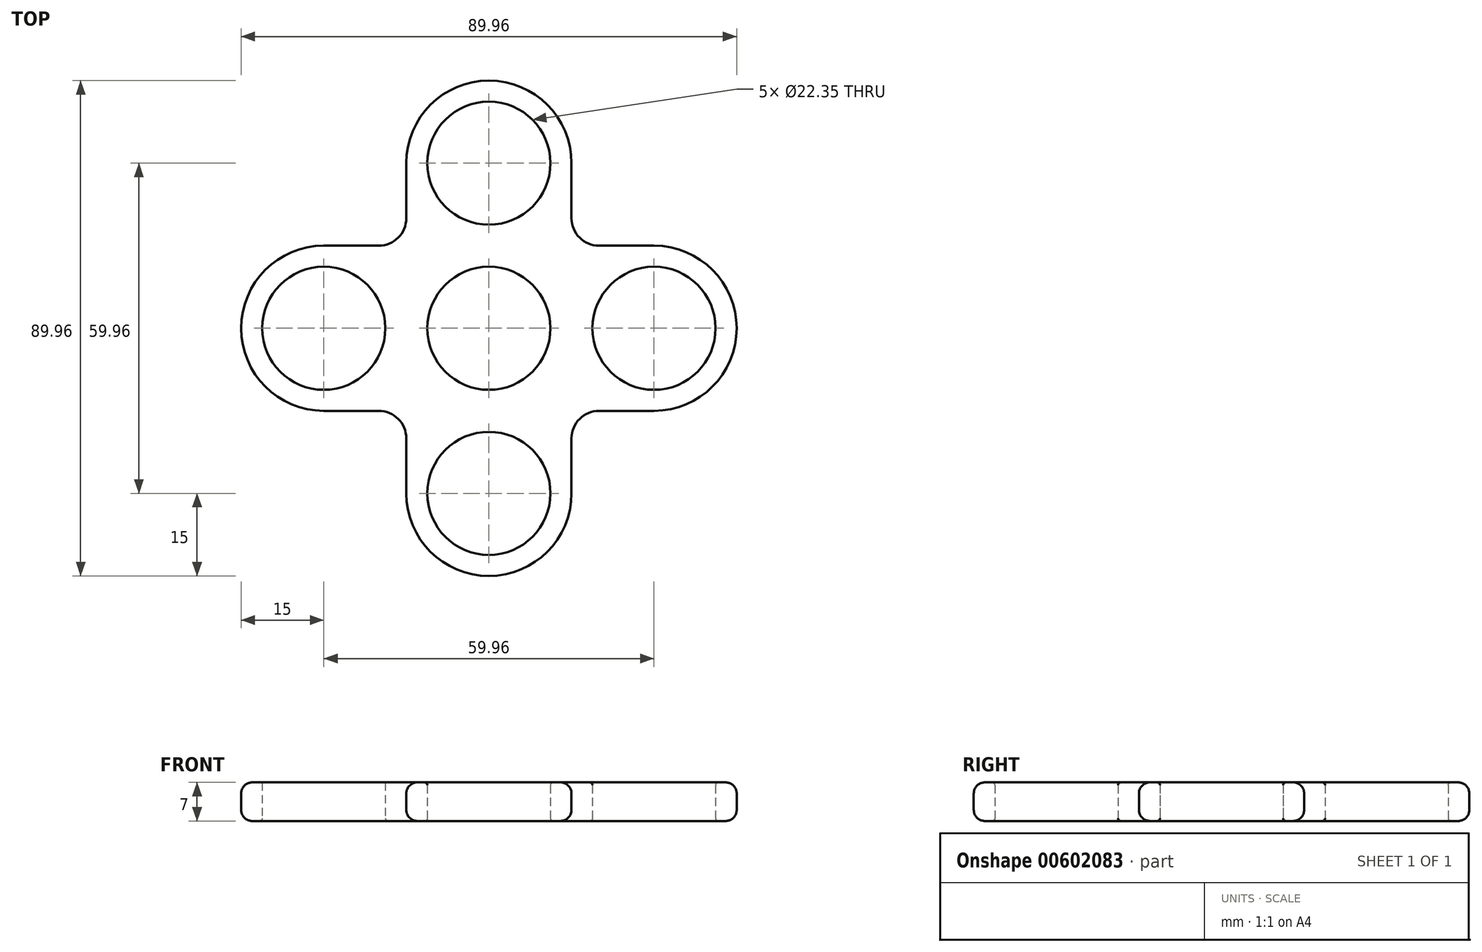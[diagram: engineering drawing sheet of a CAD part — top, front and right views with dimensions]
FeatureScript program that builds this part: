
annotation { "Feature Type Name" : "Feature", "Feature Type Description" : "" }
export const myFeature = defineFeature(function(context is Context, id is Id, definition is map)
    precondition{}
    {
        {
            var Q0;
            Q0=qCreatedBy(makeId("Top.planeOp"),FACE);
            var sketch = newSketch(context, id + "F0", { "sketchPlane" : qUnion([Q0])});
            skCircle(sketch, "E0", {"center": v(0, 29.98) * mm, "radius": 11.18 * mm});
            skLineSegment(sketch, "E1", {"start": v(0, 0) * mm, "end": v(0, 29.98) * mm, "construction": true});
            skCircle(sketch, "E2", {"center": v(0, 29.98) * mm, "radius": 15 * mm});
            skCircle(sketch, "E3", {"center": v(0, 0) * mm, "radius": 11.18 * mm});
            skLineSegment(sketch, "E4", {"start": v(-15, 29.98) * mm, "end": v(-15, 0) * mm});
            skLineSegment(sketch, "E5", {"start": v(15, 29.98) * mm, "end": v(15, 0) * mm});
            skLineSegment(sketch, "E6", {"start": v(-15, 0) * mm, "end": v(15, 0) * mm});
            skLineSegment(sketch, "E7.1.0", {"start": v(-29.98, -15) * mm, "end": v(0, -15) * mm});
            skCircle(sketch, "E7.1.1", {"center": v(-29.98, 0) * mm, "radius": 15 * mm});
            skCircle(sketch, "E7.1.2", {"center": v(-29.98, 0) * mm, "radius": 11.18 * mm});
            skLineSegment(sketch, "E7.1.3", {"start": v(-29.98, 15) * mm, "end": v(0, 15) * mm});
            skLineSegment(sketch, "E7.2.0", {"start": v(15, -29.98) * mm, "end": v(15, 0) * mm});
            skCircle(sketch, "E7.2.1", {"center": v(0, -29.98) * mm, "radius": 15 * mm});
            skCircle(sketch, "E7.2.2", {"center": v(0, -29.98) * mm, "radius": 11.18 * mm});
            skLineSegment(sketch, "E7.2.3", {"start": v(-15, -29.98) * mm, "end": v(-15, 0) * mm});
            skLineSegment(sketch, "E7.3.0", {"start": v(29.98, 15) * mm, "end": v(0, 15) * mm});
            skCircle(sketch, "E7.3.1", {"center": v(29.98, 0) * mm, "radius": 15 * mm});
            skCircle(sketch, "E7.3.2", {"center": v(29.98, 0) * mm, "radius": 11.18 * mm});
            skLineSegment(sketch, "E7.3.3", {"start": v(29.98, -15) * mm, "end": v(0, -15) * mm});
            skSolve(sketch);
        }
        {
            var Q0;
            Q0=makeQuery(id+"F0.imprint","IMPRINT",FACE,{"disambiguationData":[TD([[makeQuery(id+"F0.imprint","IMPRINT",EDGE,{"derivedFrom":sQuery(id+"F0.wireOp",EDGE,"36e7d391-d642-43d3-ac27-a5ee1db5424b.1.0")}),-1.0]])]});
            var Q1;
            {var subQ7=sQuery(id+"F0.wireOp",EDGE,"E6");var subQ10=sQuery(id+"F0.wireOp",EDGE,"E3");var subQ14=makeQuery(id+"F0.imprint","INTERSECT",VERTEX,{"disambiguationData":[OD(0.0)],"derivedFrom":[subQ10,subQ7]});Q1=makeQuery(id+"F0.imprint","IMPRINT",FACE,{"disambiguationData":[TD([[makeQuery(id+"F0.imprint","IMPRINT",EDGE,{"disambiguationData":[TD([[subQ14,-1.0]])],"derivedFrom":subQ10}),-1.0]])]});}
            var Q2;
            Q2=makeQuery(id+"F0.imprint","IMPRINT",FACE,{"disambiguationData":[TD([[makeQuery(id+"F0.imprint","IMPRINT",EDGE,{"derivedFrom":sQuery(id+"F0.wireOp",EDGE,"36e7d391-d642-43d3-ac27-a5ee1db5424b.2.0")}),-1.0]])]});
            var Q3;
            {var subQ1=sQuery(id+"F0.wireOp",EDGE,"E4");var subQ4=sQuery(id+"F0.wireOp",EDGE,"E2");var subQ5=makeQuery(id+"F0.imprint","INTERSECT",VERTEX,{"derivedFrom":[subQ4,subQ1]});Q3=makeQuery(id+"F0.imprint","IMPRINT",FACE,{"disambiguationData":[TD([[makeQuery(id+"F0.imprint","IMPRINT",EDGE,{"disambiguationData":[TD([[subQ5,-1.0]])],"derivedFrom":subQ4}),-1.0]])]});}
            var Q4;
            Q4=makeQuery(id+"F0.imprint","IMPRINT",FACE,{"disambiguationData":[TD([[makeQuery(id+"F0.imprint","IMPRINT",EDGE,{"derivedFrom":sQuery(id+"F0.wireOp",EDGE,"E0")}),-1.0]])]});
            var Q5;
            Q5=makeQuery(id+"F0.imprint","IMPRINT",FACE,{"disambiguationData":[TD([[makeQuery(id+"F0.imprint","IMPRINT",EDGE,{"derivedFrom":sQuery(id+"F0.wireOp",EDGE,"E7.1.2")}),-1.0]])]});
            var Q6;
            {var subQ10=sQuery(id+"F0.wireOp",EDGE,"E7.1.3");var subQ15=sQuery(id+"F0.wireOp",EDGE,"E2");var subQ16=makeQuery(id+"F0.imprint","INTERSECT",VERTEX,{"derivedFrom":[subQ15,subQ10]});Q6=makeQuery(id+"F0.imprint","IMPRINT",FACE,{"disambiguationData":[TD([[makeQuery(id+"F0.imprint","IMPRINT",EDGE,{"disambiguationData":[TD([[subQ16,-1.0]])],"derivedFrom":subQ15}),-1.0]])]});}
            var Q7;
            {var subQ0=sQuery(id+"F0.wireOp",EDGE,"E7.1.3");var subQ1=sQuery(id+"F0.wireOp",EDGE,"E2");var subQ2=makeQuery(id+"F0.imprint","INTERSECT",VERTEX,{"derivedFrom":[subQ1,subQ0]});Q7=makeQuery(id+"F0.imprint","IMPRINT",FACE,{"disambiguationData":[TD([[makeQuery(id+"F0.imprint","IMPRINT",EDGE,{"disambiguationData":[TD([[subQ2,-1.0]])],"derivedFrom":subQ1}),1.0]])]});}
            var Q8;
            {var subQ1=sQuery(id+"F0.wireOp",EDGE,"E4");var subQ3=sQuery(id+"F0.wireOp",EDGE,"E7.1.1");var subQ4=makeQuery(id+"F0.imprint","INTERSECT",VERTEX,{"derivedFrom":[subQ1,subQ3]});Q8=makeQuery(id+"F0.imprint","IMPRINT",FACE,{"disambiguationData":[TD([[makeQuery(id+"F0.imprint","IMPRINT",EDGE,{"disambiguationData":[TD([[subQ4,1.0]])],"derivedFrom":subQ3}),1.0]])]});}
            var Q9;
            {var subQ1=sQuery(id+"F0.wireOp",EDGE,"E6");var subQ3=sQuery(id+"F0.wireOp",EDGE,"E7.1.1");var subQ4=makeQuery(id+"F0.imprint","INTERSECT",VERTEX,{"derivedFrom":[subQ1,subQ3]});Q9=makeQuery(id+"F0.imprint","IMPRINT",FACE,{"disambiguationData":[TD([[makeQuery(id+"F0.imprint","IMPRINT",EDGE,{"disambiguationData":[TD([[subQ4,1.0]])],"derivedFrom":subQ3}),1.0]])]});}
            var Q10;
            Q10=makeQuery(id+"F0.imprint","IMPRINT",FACE,{"disambiguationData":[TD([[makeQuery(id+"F0.imprint","IMPRINT",EDGE,{"derivedFrom":sQuery(id+"F0.wireOp",EDGE,"E7.3.2")}),-1.0]])]});
            var Q11;
            {var subQ0=sQuery(id+"F0.wireOp",EDGE,"E7.3.3");var subQ1=sQuery(id+"F0.wireOp",EDGE,"E7.2.0");var subQ2=makeQuery(id+"F0.imprint","INTERSECT",VERTEX,{"derivedFrom":[subQ1,subQ0]});Q11=makeQuery(id+"F0.imprint","IMPRINT",FACE,{"disambiguationData":[TD([[makeQuery(id+"F0.imprint","IMPRINT",EDGE,{"disambiguationData":[TD([[subQ2,-1.0]])],"derivedFrom":subQ1}),-1.0]])]});}
            var Q12;
            {var subQ1=sQuery(id+"F0.wireOp",EDGE,"E6");var subQ3=sQuery(id+"F0.wireOp",EDGE,"E7.3.1");var subQ4=makeQuery(id+"F0.imprint","INTERSECT",VERTEX,{"derivedFrom":[subQ1,subQ3]});Q12=makeQuery(id+"F0.imprint","IMPRINT",FACE,{"disambiguationData":[TD([[makeQuery(id+"F0.imprint","IMPRINT",EDGE,{"disambiguationData":[TD([[subQ4,-1.0]])],"derivedFrom":subQ3}),1.0]])]});}
            var Q13;
            {var subQ1=sQuery(id+"F0.wireOp",EDGE,"E5");var subQ3=sQuery(id+"F0.wireOp",EDGE,"E7.3.1");var subQ4=makeQuery(id+"F0.imprint","INTERSECT",VERTEX,{"derivedFrom":[subQ1,subQ3]});Q13=makeQuery(id+"F0.imprint","IMPRINT",FACE,{"disambiguationData":[TD([[makeQuery(id+"F0.imprint","IMPRINT",EDGE,{"disambiguationData":[TD([[subQ4,-1.0]])],"derivedFrom":subQ3}),1.0]])]});}
            var Q14;
            {var subQ0=sQuery(id+"F0.wireOp",EDGE,"E7.3.0");var subQ1=sQuery(id+"F0.wireOp",EDGE,"E5");var subQ2=makeQuery(id+"F0.imprint","INTERSECT",VERTEX,{"derivedFrom":[subQ1,subQ0]});Q14=makeQuery(id+"F0.imprint","IMPRINT",FACE,{"disambiguationData":[TD([[makeQuery(id+"F0.imprint","IMPRINT",EDGE,{"disambiguationData":[TD([[subQ2,-1.0]])],"derivedFrom":subQ1}),1.0]])]});}
            var Q15;
            {var subQ0=sQuery(id+"F0.wireOp",EDGE,"E5");var subQ1=sQuery(id+"F0.wireOp",EDGE,"E2");var subQ2=makeQuery(id+"F0.imprint","INTERSECT",VERTEX,{"derivedFrom":[subQ1,subQ0]});Q15=makeQuery(id+"F0.imprint","IMPRINT",FACE,{"disambiguationData":[TD([[makeQuery(id+"F0.imprint","IMPRINT",EDGE,{"disambiguationData":[TD([[subQ2,1.0]])],"derivedFrom":subQ1}),-1.0]])]});}
            var Q16;
            Q16=makeQuery(id+"F0.imprint","IMPRINT",FACE,{"disambiguationData":[TD([[makeQuery(id+"F0.imprint","IMPRINT",EDGE,{"derivedFrom":sQuery(id+"F0.wireOp",EDGE,"E7.2.2")}),-1.0]])]});
            var Q17;
            {var subQ0=sQuery(id+"F0.wireOp",EDGE,"E7.2.1");var subQ1=sQuery(id+"F0.wireOp",EDGE,"E7.2.0");var subQ2=makeQuery(id+"F0.imprint","INTERSECT",VERTEX,{"derivedFrom":[subQ1,subQ0]});Q17=makeQuery(id+"F0.imprint","IMPRINT",FACE,{"disambiguationData":[TD([[makeQuery(id+"F0.imprint","IMPRINT",EDGE,{"disambiguationData":[TD([[subQ2,-1.0]])],"derivedFrom":subQ1}),1.0]])]});}
            var Q18;
            {var subQ0=sQuery(id+"F0.wireOp",EDGE,"E7.3.3");var subQ1=sQuery(id+"F0.wireOp",EDGE,"E7.1.0");var subQ2=makeQuery(id+"F0.imprint","INTERSECT",VERTEX,{"derivedFrom":[subQ1,subQ0]});Q18=makeQuery(id+"F0.imprint","IMPRINT",FACE,{"disambiguationData":[TD([[makeQuery(id+"F0.imprint","IMPRINT",EDGE,{"disambiguationData":[TD([[subQ2,1.0]])],"derivedFrom":subQ1}),1.0]])]});}
            var Q19;
            {var subQ0=sQuery(id+"F0.wireOp",EDGE,"E7.2.3");var subQ1=sQuery(id+"F0.wireOp",EDGE,"E7.1.0");var subQ2=makeQuery(id+"F0.imprint","INTERSECT",VERTEX,{"derivedFrom":[subQ1,subQ0]});Q19=makeQuery(id+"F0.imprint","IMPRINT",FACE,{"disambiguationData":[TD([[makeQuery(id+"F0.imprint","IMPRINT",EDGE,{"disambiguationData":[TD([[subQ2,-1.0]])],"derivedFrom":subQ1}),-1.0]])]});}
            var Q20;
            {var subQ0=sQuery(id+"F0.wireOp",EDGE,"E7.1.1");var subQ1=sQuery(id+"F0.wireOp",EDGE,"E7.1.0");var subQ2=makeQuery(id+"F0.imprint","INTERSECT",VERTEX,{"derivedFrom":[subQ1,subQ0]});Q20=makeQuery(id+"F0.imprint","IMPRINT",FACE,{"disambiguationData":[TD([[makeQuery(id+"F0.imprint","IMPRINT",EDGE,{"disambiguationData":[TD([[subQ2,-1.0]])],"derivedFrom":subQ1}),1.0]])]});}
            var Q21;
            {var subQ0=sQuery(id+"F0.wireOp",EDGE,"E7.1.3");var subQ1=sQuery(id+"F0.wireOp",EDGE,"E4");var subQ2=makeQuery(id+"F0.imprint","INTERSECT",VERTEX,{"derivedFrom":[subQ1,subQ0]});Q21=makeQuery(id+"F0.imprint","IMPRINT",FACE,{"disambiguationData":[TD([[makeQuery(id+"F0.imprint","IMPRINT",EDGE,{"disambiguationData":[TD([[subQ2,-1.0]])],"derivedFrom":subQ1}),-1.0]])]});}
            extrude(context, id + "F1", {"entities" : qUnion([Q0, Q1, Q2, Q3, Q4, Q5, Q6, Q7, Q8, Q9, Q10, Q11, Q12, Q13, Q14, Q15, Q16, Q17, Q18, Q19, Q20, Q21]), "depth" : 7 * mm});
        }
        {
            var Q0;
            Q0=makeQuery(id+"F1.opExtrude","SWEPT_EDGE",EDGE,{"disambiguationData":[OSD([sQuery(id+"F0.wireOp",EDGE,"E4"),sQuery(id+"F0.wireOp",EDGE,"36e7d391-d642-43d3-ac27-a5ee1db5424b.1.2")])]});
            var Q1;
            Q1=makeQuery(id+"F1.opExtrude","SWEPT_EDGE",EDGE,{"disambiguationData":[OSD([sQuery(id+"F0.wireOp",EDGE,"E5"),sQuery(id+"F0.wireOp",EDGE,"36e7d391-d642-43d3-ac27-a5ee1db5424b.2.3")])]});
            var Q2;
            Q2=makeQuery(id+"F1.opExtrude","SWEPT_EDGE",EDGE,{"disambiguationData":[OSD([sQuery(id+"F0.wireOp",EDGE,"36e7d391-d642-43d3-ac27-a5ee1db5424b.1.3"),sQuery(id+"F0.wireOp",EDGE,"36e7d391-d642-43d3-ac27-a5ee1db5424b.2.2")])]});
            var Q3;
            Q3=makeQuery(id+"F1.opExtrude","SWEPT_EDGE",EDGE,{"disambiguationData":[OSD([sQuery(id+"F0.wireOp",EDGE,"E7.2.0"),sQuery(id+"F0.wireOp",EDGE,"E7.3.3")])]});
            var Q4;
            Q4=makeQuery(id+"F1.opExtrude","SWEPT_EDGE",EDGE,{"disambiguationData":[OSD([sQuery(id+"F0.wireOp",EDGE,"E7.1.0"),sQuery(id+"F0.wireOp",EDGE,"E7.2.3")])]});
            fillet(context, id + "F2", {"entities" : qUnion([Q0, Q1, Q2, Q3, Q4]), "radius" : 5 * mm, "tangentPropagation" : true, "allowEdgeOverflow" : false});
        }
        {
            var Q0;
            Q0=makeQuery(id+"F1.opExtrude","CAP_EDGE",EDGE,{"disambiguationData":[OSD([sQuery(id+"F0.wireOp",EDGE,"E0")])],"isStart":false});
            var Q1;
            Q1=makeQuery(id+"F1.opExtrude","CAP_EDGE",EDGE,{"disambiguationData":[OSD([sQuery(id+"F0.wireOp",EDGE,"E3")])],"isStart":false});
            var Q2;
            Q2=makeQuery(id+"F1.opExtrude","CAP_EDGE",EDGE,{"disambiguationData":[OSD([sQuery(id+"F0.wireOp",EDGE,"36e7d391-d642-43d3-ac27-a5ee1db5424b.1.0")])],"isStart":false});
            var Q3;
            Q3=makeQuery(id+"F1.opExtrude","CAP_EDGE",EDGE,{"disambiguationData":[OSD([sQuery(id+"F0.wireOp",EDGE,"36e7d391-d642-43d3-ac27-a5ee1db5424b.2.0")])],"isStart":false});
            var Q4;
            Q4=makeQuery(id+"F1.opExtrude","CAP_EDGE",EDGE,{"disambiguationData":[OSD([sQuery(id+"F0.wireOp",EDGE,"36e7d391-d642-43d3-ac27-a5ee1db5424b.1.0")])],"isStart":true});
            var Q5;
            Q5=makeQuery(id+"F1.opExtrude","CAP_EDGE",EDGE,{"disambiguationData":[OSD([sQuery(id+"F0.wireOp",EDGE,"E0")])],"isStart":true});
            var Q6;
            Q6=makeQuery(id+"F1.opExtrude","CAP_EDGE",EDGE,{"disambiguationData":[OSD([sQuery(id+"F0.wireOp",EDGE,"36e7d391-d642-43d3-ac27-a5ee1db5424b.2.0")])],"isStart":true});
            var Q7;
            Q7=makeQuery(id+"F1.opExtrude","CAP_EDGE",EDGE,{"disambiguationData":[OSD([sQuery(id+"F0.wireOp",EDGE,"E3")])],"isStart":true});
            var Q8;
            Q8=makeQuery(id+"F1.opExtrude","CAP_EDGE",EDGE,{"disambiguationData":[OSD([sQuery(id+"F0.wireOp",EDGE,"E7.2.2")])],"isStart":false});
            var Q9;
            Q9=makeQuery(id+"F1.opExtrude","CAP_EDGE",EDGE,{"disambiguationData":[OSD([sQuery(id+"F0.wireOp",EDGE,"E7.1.2")])],"isStart":true});
            var Q10;
            Q10=makeQuery(id+"F1.opExtrude","CAP_EDGE",EDGE,{"disambiguationData":[OSD([sQuery(id+"F0.wireOp",EDGE,"E7.3.2")])],"isStart":true});
            var Q11;
            Q11=makeQuery(id+"F1.opExtrude","CAP_EDGE",EDGE,{"disambiguationData":[OSD([sQuery(id+"F0.wireOp",EDGE,"E7.2.2")])],"isStart":true});
            var Q12;
            Q12=makeQuery(id+"F1.opExtrude","CAP_EDGE",EDGE,{"disambiguationData":[OSD([sQuery(id+"F0.wireOp",EDGE,"E7.3.2")])],"isStart":false});
            fillet(context, id + "F3", {"entities" : qUnion([Q0, Q1, Q2, Q3, Q4, Q5, Q6, Q7, Q8, Q9, Q10, Q11, Q12]), "radius" : .5 * mm, "tangentPropagation" : true, "allowEdgeOverflow" : false});
        }
        {
            var Q0;
            Q0=makeQuery(id+"F1.opExtrude","SWEPT_FACE",FACE,{"disambiguationData":[OSD([sQuery(id+"F0.wireOp",EDGE,"36e7d391-d642-43d3-ac27-a5ee1db5424b.1.3")])]});
            var Q1;
            Q1=makeQuery(id+"F2.opFillet","BLEND_FACE",FACE,{"disambiguationData":[OSD([sQuery(id+"F0.wireOp",EDGE,"36e7d391-d642-43d3-ac27-a5ee1db5424b.1.3"),sQuery(id+"F0.wireOp",EDGE,"36e7d391-d642-43d3-ac27-a5ee1db5424b.2.2")])]});
            var Q2;
            Q2=makeQuery(id+"F1.opExtrude","SWEPT_FACE",FACE,{"disambiguationData":[OSD([sQuery(id+"F0.wireOp",EDGE,"36e7d391-d642-43d3-ac27-a5ee1db5424b.2.2")])]});
            var Q3;
            Q3=makeQuery(id+"F1.opExtrude","SWEPT_FACE",FACE,{"disambiguationData":[OSD([sQuery(id+"F0.wireOp",EDGE,"36e7d391-d642-43d3-ac27-a5ee1db5424b.2.1")])]});
            var Q4;
            Q4=makeQuery(id+"F1.opExtrude","SWEPT_FACE",FACE,{"disambiguationData":[OSD([sQuery(id+"F0.wireOp",EDGE,"36e7d391-d642-43d3-ac27-a5ee1db5424b.1.1")])]});
            var Q5;
            Q5=makeQuery(id+"F1.opExtrude","SWEPT_FACE",FACE,{"disambiguationData":[OSD([sQuery(id+"F0.wireOp",EDGE,"36e7d391-d642-43d3-ac27-a5ee1db5424b.1.2")])]});
            var Q6;
            Q6=makeQuery(id+"F2.opFillet","BLEND_FACE",FACE,{"disambiguationData":[OSD([sQuery(id+"F0.wireOp",EDGE,"E4"),sQuery(id+"F0.wireOp",EDGE,"36e7d391-d642-43d3-ac27-a5ee1db5424b.1.2")])]});
            var Q7;
            Q7=makeQuery(id+"F1.opExtrude","SWEPT_FACE",FACE,{"disambiguationData":[OSD([sQuery(id+"F0.wireOp",EDGE,"E4")])]});
            var Q8;
            Q8=makeQuery(id+"F1.opExtrude","SWEPT_FACE",FACE,{"disambiguationData":[OSD([sQuery(id+"F0.wireOp",EDGE,"E2")])]});
            var Q9;
            Q9=makeQuery(id+"F1.opExtrude","SWEPT_FACE",FACE,{"disambiguationData":[OSD([sQuery(id+"F0.wireOp",EDGE,"E5")])]});
            var Q10;
            Q10=makeQuery(id+"F2.opFillet","BLEND_FACE",FACE,{"disambiguationData":[OSD([sQuery(id+"F0.wireOp",EDGE,"E5"),sQuery(id+"F0.wireOp",EDGE,"36e7d391-d642-43d3-ac27-a5ee1db5424b.2.3")])]});
            var Q11;
            Q11=makeQuery(id+"F1.opExtrude","SWEPT_FACE",FACE,{"disambiguationData":[OSD([sQuery(id+"F0.wireOp",EDGE,"36e7d391-d642-43d3-ac27-a5ee1db5424b.2.3")])]});
            var Q12;
            Q12=makeQuery(id+"F1.opExtrude","CAP_EDGE",EDGE,{"disambiguationData":[OSD([sQuery(id+"F0.wireOp",EDGE,"E7.2.1")])],"isStart":false});
            var Q13;
            Q13=makeQuery(id+"F1.opExtrude","CAP_EDGE",EDGE,{"disambiguationData":[OSD([sQuery(id+"F0.wireOp",EDGE,"E7.2.1")])],"isStart":true});
            fillet(context, id + "F4", {"entities" : qUnion([Q0, Q1, Q2, Q3, Q4, Q5, Q6, Q7, Q8, Q9, Q10, Q11, Q12, Q13]), "radius" : 2 * mm, "tangentPropagation" : true, "allowEdgeOverflow" : false});
        }
    });
